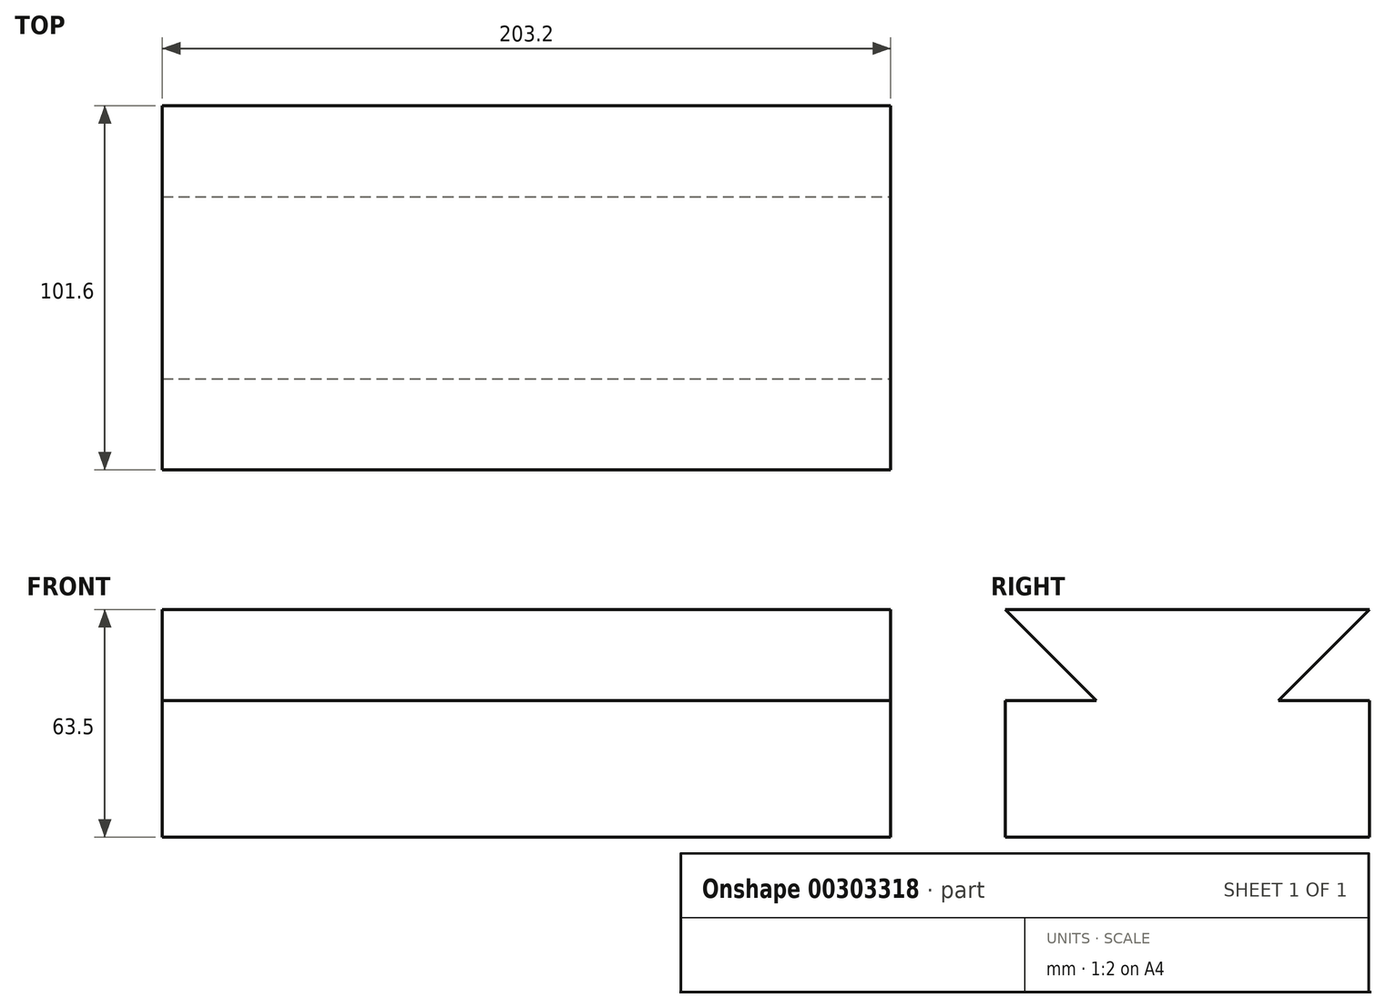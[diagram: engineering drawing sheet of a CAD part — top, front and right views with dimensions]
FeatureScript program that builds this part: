
annotation { "Feature Type Name" : "Feature", "Feature Type Description" : "" }
export const myFeature = defineFeature(function(context is Context, id is Id, definition is map)
    precondition{}
    {
        {
            var Q0;
            Q0=qCreatedBy(makeId("Right.planeOp"),FACE);
            var sketch = newSketch(context, id + "F0", { "sketchPlane" : qUnion([Q0])});
            skLineSegment(sketch, "E0", {"start": v(0, 0) * mm, "end": v(101.6, 0) * mm});
            skLineSegment(sketch, "E1", {"start": v(101.6, 0) * mm, "end": v(101.6, 38.1) * mm});
            skLineSegment(sketch, "E2", {"start": v(101.6, 38.1) * mm, "end": v(76.2, 38.1) * mm});
            skLineSegment(sketch, "E3", {"start": v(0, 0) * mm, "end": v(0, 38.1) * mm});
            skLineSegment(sketch, "E4", {"start": v(0, 38.1) * mm, "end": v(25.4, 38.1) * mm});
            skLineSegment(sketch, "E5", {"start": v(25.4, 38.1) * mm, "end": v(0, 63.5) * mm});
            skLineSegment(sketch, "E6", {"start": v(0, 63.5) * mm, "end": v(101.6, 63.5) * mm});
            skLineSegment(sketch, "E7", {"start": v(101.6, 63.5) * mm, "end": v(76.2, 38.1) * mm});
            skSolve(sketch);
        }
        {
            var Q0;
            Q0 = qSketchRegion(id + "F0", true);
            extrude(context, id + "F1", {"entities" : qUnion([Q0]), "oppositeDirection" : true, "depth" : 203.2 * mm});
        }
    });
